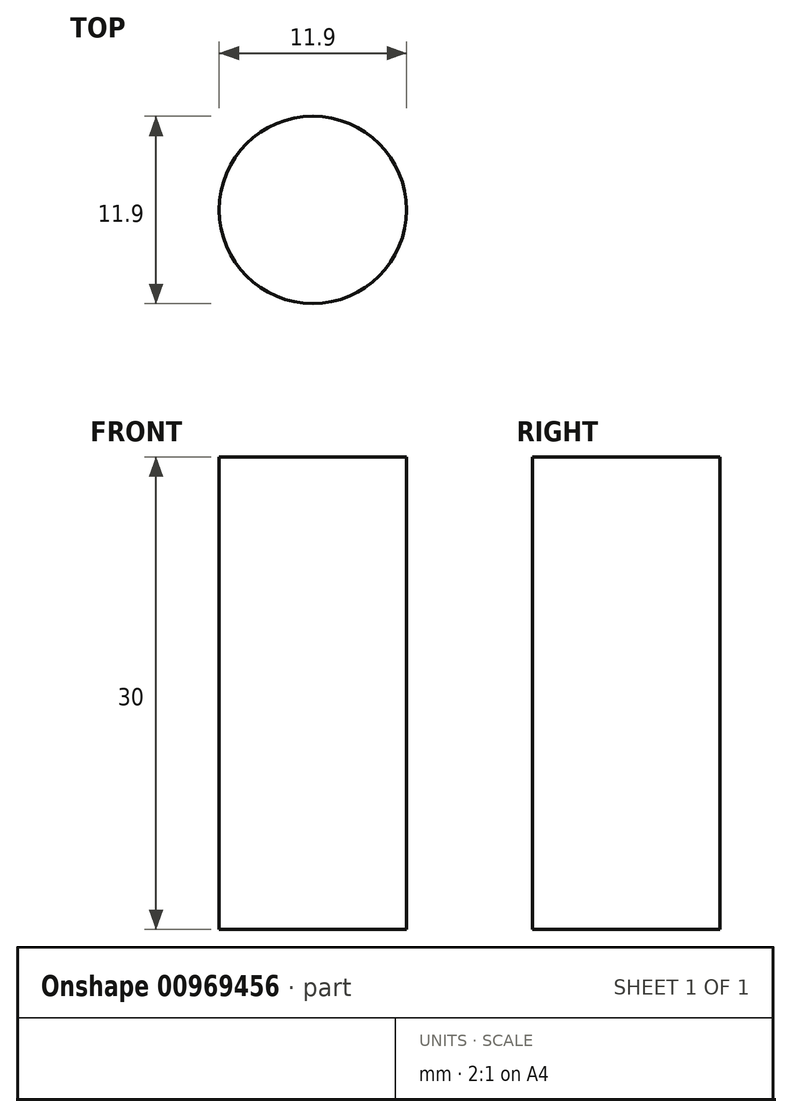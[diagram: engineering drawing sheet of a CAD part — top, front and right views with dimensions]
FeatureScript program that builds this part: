
annotation { "Feature Type Name" : "Feature", "Feature Type Description" : "" }
export const myFeature = defineFeature(function(context is Context, id is Id, definition is map)
    precondition{}
    {
        {
            var Q0;
            Q0=qCreatedBy(makeId("Top.planeOp"),FACE);
            var sketch = newSketch(context, id + "F0", { "sketchPlane" : qUnion([Q0])});
            skCircle(sketch, "E0", {"center": v(0, 0) * mm, "radius": 5.95 * mm});
            skSolve(sketch);
        }
        {
            var Q0;
            Q0 = qSketchRegion(id + "F0", true);
            extrude(context, id + "F1", {"entities" : qUnion([Q0]), "endBound" : BoundingType.SYMMETRIC, "depth" : 30 * mm, "offsetDistance" : 25 * mm});
        }
    });
